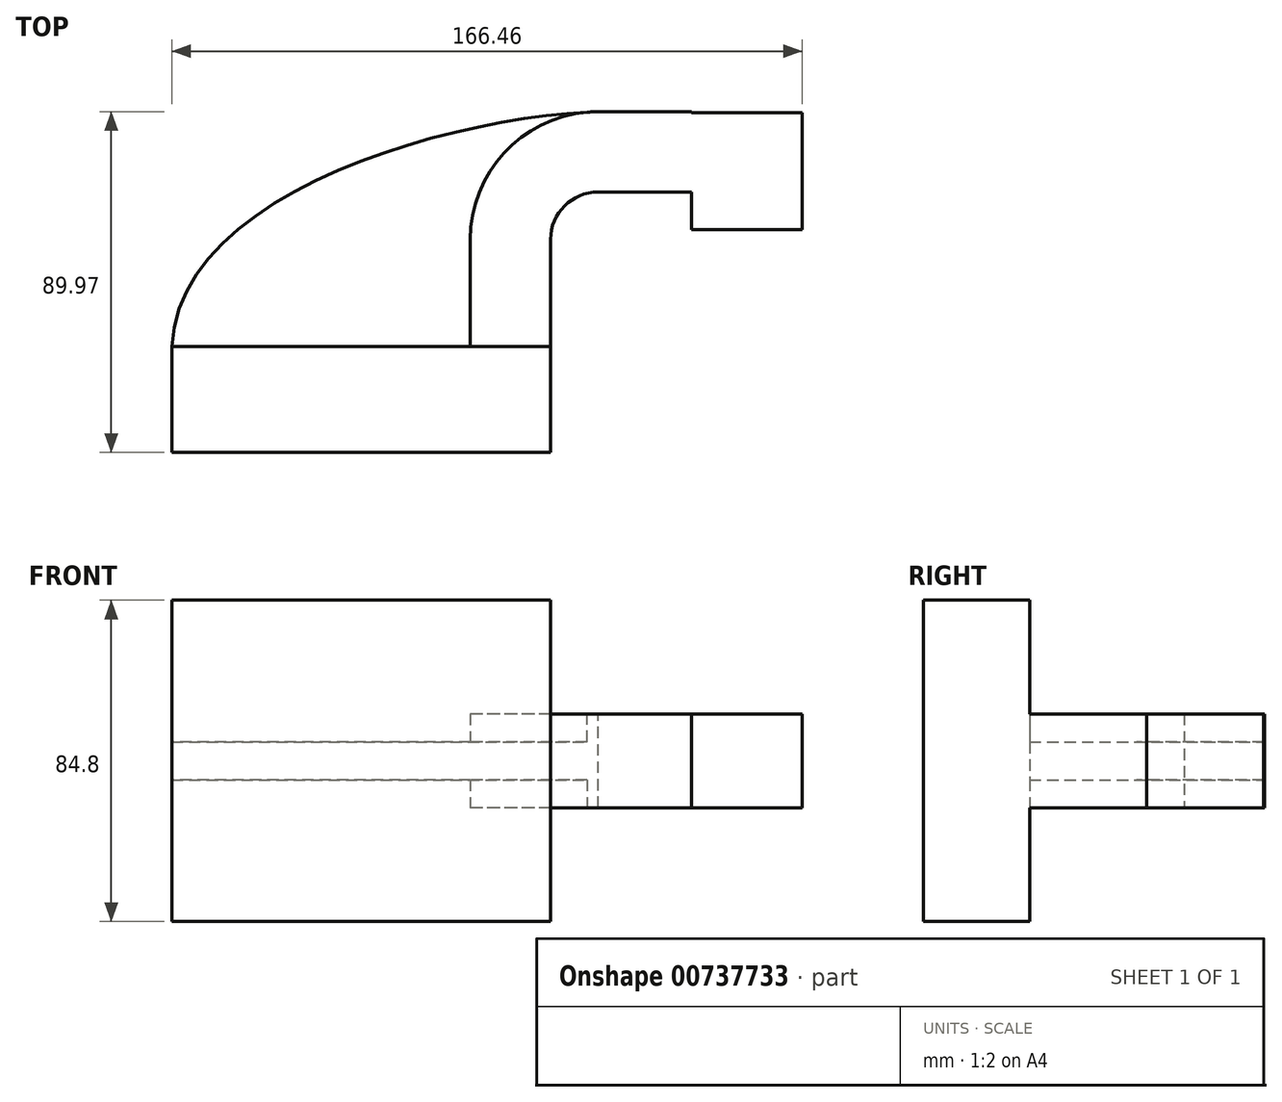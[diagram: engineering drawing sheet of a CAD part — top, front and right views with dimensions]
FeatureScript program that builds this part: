
annotation { "Feature Type Name" : "Feature", "Feature Type Description" : "" }
export const myFeature = defineFeature(function(context is Context, id is Id, definition is map)
    precondition{}
    {
        {
            var Q0;
            Q0=qCreatedBy(makeId("Top.planeOp"),FACE);
            var sketch = newSketch(context, id + "F0", { "sketchPlane" : qUnion([Q0])});
            skLineSegment(sketch, "E0.bottom", {"start": v(50, -14) * mm, "end": v(-50, -14) * mm});
            skLineSegment(sketch, "E0.top", {"start": v(50, 14) * mm, "end": v(-50, 14) * mm});
            skLineSegment(sketch, "E0.left", {"start": v(50, -14) * mm, "end": v(50, 14) * mm});
            skLineSegment(sketch, "E0.right", {"start": v(-50, -14) * mm, "end": v(-50, 14) * mm});
            skPoint(sketch, "E0.middle", {"position": v(0, 0) * mm});
            skLineSegment(sketch, "E1.bottom", {"start": v(145.66, 44.9) * mm, "end": v(87.25, 44.9) * mm});
            skLineSegment(sketch, "E1.top", {"start": v(145.66, 77.1) * mm, "end": v(87.25, 77.1) * mm});
            skLineSegment(sketch, "E1.left", {"start": v(145.66, 44.9) * mm, "end": v(145.66, 77.1) * mm});
            skLineSegment(sketch, "E1.right", {"start": v(87.25, 44.9) * mm, "end": v(87.25, 77.1) * mm});
            skPoint(sketch, "E1.middle", {"position": v(116.46, 61) * mm});
            skLineSegment(sketch, "E2", {"start": v(50, 14) * mm, "end": v(50, 42.24) * mm});
            skArc(sketch, "E3", {"start": v(50, 42.24) * mm, "mid": v(53.67, 51.1) * mm, "end": v(62.53, 54.77) * mm});
            skLineSegment(sketch, "E4", {"start": v(62.53, 54.77) * mm, "end": v(116.46, 54.77) * mm});
            skLineSegment(sketch, "E5.0", {"start": v(62.53, 75.97) * mm, "end": v(116.46, 75.97) * mm});
            skArc(sketch, "E5.1", {"start": v(28.8, 42.24) * mm, "mid": v(38.68, 66.1) * mm, "end": v(62.53, 75.97) * mm});
            skLineSegment(sketch, "E5.2", {"start": v(28.8, 14) * mm, "end": v(28.8, 42.24) * mm});
            skLineSegment(sketch, "E6.0", {"start": v(62.53, 75.68) * mm, "end": v(116.46, 75.68) * mm});
            skArc(sketch, "E6.1", {"start": v(29.45, 37.36) * mm, "mid": v(37.22, 64.1) * mm, "end": v(62.53, 75.68) * mm});
            skLineSegment(sketch, "E7", {"start": v(116.46, 77.1) * mm, "end": v(116.46, 44.9) * mm});
            skFitSpline(sketch, "E8", {"points": [v(-50, 14) * mm, v(62.53, 75.97) * mm], "startDerivative": vector(6.1, 122.7) * mm, "endDerivative": vector(115.84, 3.7) * mm});
            skSolve(sketch);
        }
        {
            var Q0;
            Q0=makeQuery(id+"F0.imprint","IMPRINT",FACE,{"disambiguationData":[TD([[makeQuery(id+"F0.imprint","IMPRINT",EDGE,{"derivedFrom":sQuery(id+"F0.wireOp",EDGE,"E0.bottom")}),-1.0]])]});
            extrude(context, id + "F1", {"entities" : qUnion([Q0]), "endBound" : BoundingType.SYMMETRIC, "depth" : 84.8 * mm, "offsetDistance" : 25 * mm});
        }
        {
            var Q0;
            {var subQ0=sQuery(id+"F0.wireOp",EDGE,"E2");Q0=makeQuery(id+"F0.imprint","IMPRINT",FACE,{"disambiguationData":[TD([[makeQuery(id+"F0.imprint","IMPRINT",EDGE,{"derivedFrom":subQ0}),1.0]])]});}
            var Q1;
            {var subQ0=sQuery(id+"F0.wireOp",EDGE,"E4");var subQ1=sQuery(id+"F0.wireOp",EDGE,"E1.right");var subQ2=makeQuery(id+"F0.imprint","INTERSECT",VERTEX,{"derivedFrom":[subQ1,subQ0]});Q1=makeQuery(id+"F0.imprint","IMPRINT",FACE,{"disambiguationData":[TD([[makeQuery(id+"F0.imprint","IMPRINT",EDGE,{"disambiguationData":[TD([[subQ2,-1.0]])],"derivedFrom":subQ1}),-1.0]])]});}
            var Q2;
            {var subQ0=sQuery(id+"F0.wireOp",EDGE,"E1.right");var subQ1=sQuery(id+"F0.wireOp",EDGE,"E1.bottom");var subQ2=makeQuery(id+"F0.imprint","INTERSECT",VERTEX,{"derivedFrom":[subQ1,subQ0]});Q2=makeQuery(id+"F0.imprint","IMPRINT",FACE,{"disambiguationData":[TD([[makeQuery(id+"F0.imprint","IMPRINT",EDGE,{"disambiguationData":[TD([[subQ2,1.0]])],"derivedFrom":subQ1}),-1.0]])]});}
            extrude(context, id + "F2", {"entities" : qUnion([Q0, Q1, Q2]), "operationType" : NewBodyOperationType.ADD, "endBound" : BoundingType.SYMMETRIC, "depth" : 24.8 * mm, "offsetDistance" : 25 * mm});
        }
        {
            var Q0;
            {var subQ3=sQuery(id+"F0.wireOp",EDGE,"E5.2");Q0=makeQuery(id+"F0.imprint","IMPRINT",FACE,{"disambiguationData":[TD([[makeQuery(id+"F0.imprint","IMPRINT",EDGE,{"derivedFrom":subQ3}),1.0]])]});}
            extrude(context, id + "F3", {"entities" : qUnion([Q0]), "operationType" : NewBodyOperationType.ADD, "endBound" : BoundingType.SYMMETRIC, "depth" : 10 * mm, "offsetDistance" : 25 * mm});
        }
    });
